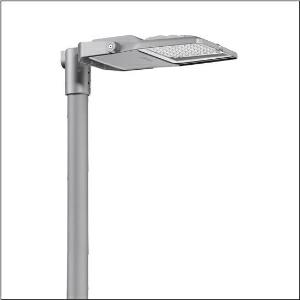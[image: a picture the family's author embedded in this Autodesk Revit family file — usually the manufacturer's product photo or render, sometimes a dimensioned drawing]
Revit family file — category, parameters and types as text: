
# Revit family: floodlight_fl_21_mini___pl61_5xa7776d2c3a_4c8f
name_source: partatom
category: Lighting Fixtures
units: mm (PartAtom-declared; Revit-internal decimal feet)

## family parameters
Cut with Voids When Loaded = No
Host = Face
Light Source = No
Part Type = Normal
Room Calculation Point = No
Round Connector Dimension = Use Diameter
Shared = No

## types (1)
- --- (1 x LED, 17510 lm, 142.9 W, 3000K)
    Apparent Load = 143 VA
    CIE Flux Codes = 33 65 98 100 100
    Color Rendering = 70
    Color Temperature = 3000K
    Default Elevation = 1800 mm
    Description = Floodlight FL 21 mini, floodlight, primary light control with lens, of PMMA, primary optical cover: protective disc, of toughened safety glass, transparent, light distribution: PL61, light emission: direct distribution, installation type: surface-mounted, LED, High Power LED, rated luminous flux: 17.510lm, luminous efficacy: 123lm/W, light colour: 730, colour temperature: 3000K, control: flexible luminous flux parameterisation, time-dependent luminous flux control, constant luminous flux control, overheat protection, pre-setting: logarithmic dimming characteristic, with terminal, 6-pole, mains connection: 220..240V, AC, 50/60Hz, start of lifetime: 143W, end of service life: 151W, reduction: 63W, luminaire housing, of diecast aluminium, powder-coated, Siteco® metallic grey (DB 702S), corrosivity category C5 mid according to DIN EN ISO 12944, sealing non-destructively replaceable, please order mast flange separately, mast bracket, of steel, galvanised, powder-coated, Siteco® metallic grey (DB 702S), Smart Interface below and above, protection rating (complete): IP66, insulation class (complete): insulation class II (safety insulation), certification: CE, ENEC, VDE, protection symbol: D, impact resistance: IK08, permissible operating ambient temperature: -40..+40°C, permissible operating ambient temperature for outdoor applications: -40..+50°C, standard: DIN EN 12944, LABS conformity tested according to VDMA 24364:2018-05, packaging unit: 1 piece

Light Distribution: PL61
    Height = 70 mm
    Lamp = 1 x LED
    Lamp Light Flux = 17510 lm
    Lamp Power = 142.9 W
    Lamp count = 1
    Length = 485 mm
    Luminous efficacy = 123 lm/W
    Manufacturer = Siteco
    ModVariant = No
    Model = 5XA7776D2C3A
    Number of Poles = 1
    OnlyDefault = Yes
    Power Factor = 1
    Product Name = Floodlight FL 21 mini | PL61
    Product group = floodlight | pylon annexe
    ProductGroupID = 6200
    Protection Class = Protection class II
    Protection Degree = IP 66
    RLX_Detail_Level = 1
    RLX_Emergency_Light_Flux = 0 lm
    RLX_Emergency_Type = 0
    RLX_Emergency_Type_DB = No
    RlxData = <blob elided: 101433 chars, md5=723e25d7>
    Socket = socket
    Standby Power = 0 W
    System Light Flux = 17510 lm
    System Power = 143 W
    Type Comments = factory setting: luminous flux: 100 % | dim-lin: 254 | 730 mA
    Type Image = l_1007125.jpg
    URL = http://relux.com
    VarID = @adj_142963
    Voltage = 0 V
    Weight = 0.00 kg
    Width = 337 mm

## geometry (parser evidence)
native form markers: Blend x4, Sweep x11
no freeform markers — native parametric forms only
